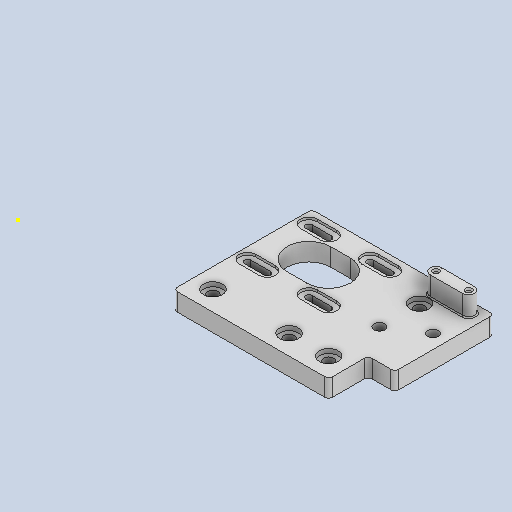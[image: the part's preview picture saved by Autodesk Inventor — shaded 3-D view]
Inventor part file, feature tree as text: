
AUTODESK INVENTOR PART (.ipt)
format: ipt  version: 2024.2 (Build 282272000, 272)  size: 404,992 bytes
history: native  units: in
note: dims shown in document units (in); Inventor stores cm internally (conversion verified against a paired STEP export)
features: sketch x1, other x1
ambient origin geometry x8: Origin, YZ Plane, XZ Plane, XY Plane, X Axis, Y Axis, Z Axis, Center Point
bodies: Solid1 (feature_tree)
feature tree (2):
  sketch  "Sketch1"
  other  "Cut-Extrude7"
